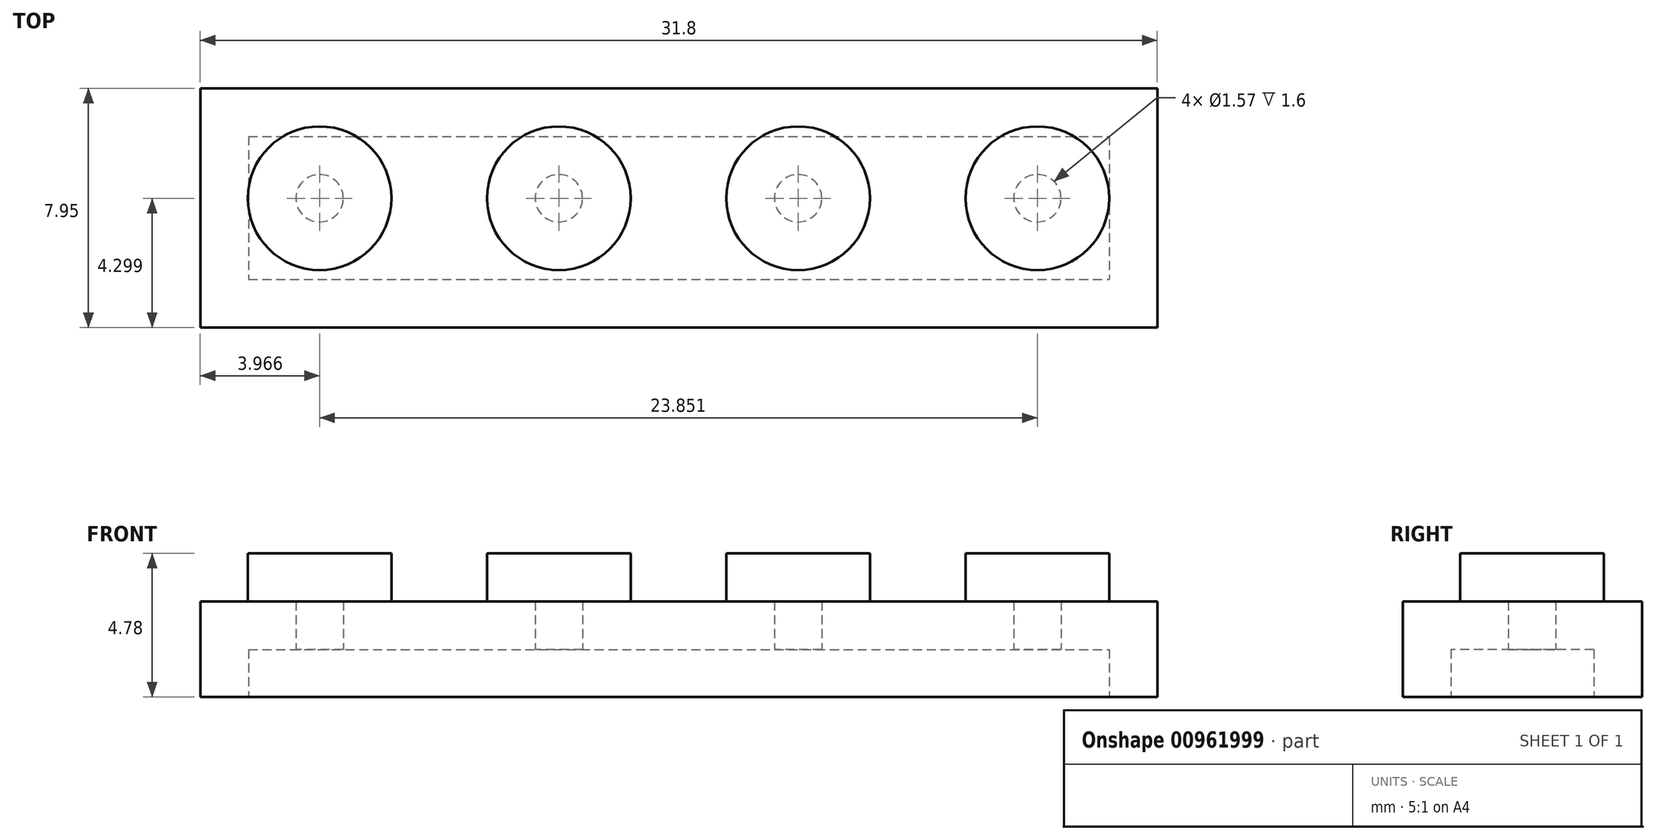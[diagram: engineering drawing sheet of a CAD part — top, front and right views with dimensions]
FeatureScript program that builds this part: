
annotation { "Feature Type Name" : "Feature", "Feature Type Description" : "" }
export const myFeature = defineFeature(function(context is Context, id is Id, definition is map)
    precondition{}
    {
        {
            var Q0;
            Q0=qCreatedBy(makeId("Top.planeOp"),FACE);
            var sketch = newSketch(context, id + "F0", { "sketchPlane" : qUnion([Q0])});
            skLineSegment(sketch, "E0.bottom", {"start": v(-20.76, 1.46) * mm, "end": v(11.04, 1.46) * mm});
            skLineSegment(sketch, "E0.top", {"start": v(-20.76, -6.49) * mm, "end": v(11.04, -6.49) * mm});
            skLineSegment(sketch, "E0.left", {"start": v(-20.76, 1.46) * mm, "end": v(-20.76, -6.49) * mm});
            skLineSegment(sketch, "E0.right", {"start": v(11.04, 1.46) * mm, "end": v(11.04, -6.49) * mm});
            skCircle(sketch, "E1", {"center": v(-16.8, -2.2) * mm, "radius": 2.39 * mm});
            skCircle(sketch, "E2.1.0.0", {"center": v(-8.84, -2.2) * mm, "radius": 2.39 * mm});
            skCircle(sketch, "E2.2.0.0", {"center": v(-0.9, -2.2) * mm, "radius": 2.39 * mm});
            skLineSegment(sketch, "E2.direction1", {"start": v(-16.8, -2.2) * mm, "end": v(-8.84, -2.2) * mm, "construction": true});
            skCircle(sketch, "E3.1.0.0", {"center": v(7.06, -2.2) * mm, "radius": 2.39 * mm});
            skLineSegment(sketch, "E3.direction1", {"start": v(-0.9, -2.2) * mm, "end": v(7.06, -2.2) * mm, "construction": true});
            skSolve(sketch);
        }
        {
            var Q0;
            Q0=makeQuery(id+"F0.imprint","IMPRINT",FACE,{"disambiguationData":[TD([[makeQuery(id+"F0.imprint","IMPRINT",EDGE,{"derivedFrom":sQuery(id+"F0.wireOp",EDGE,"E0.bottom")}),-1.0]])]});
            extrude(context, id + "F1", {"entities" : qUnion([Q0]), "depth" : 3.17 * mm, "offsetDistance" : 25.4 * mm});
        }
        {
            var Q0;
            Q0=makeQuery(id+"F0.imprint","IMPRINT",FACE,{"disambiguationData":[TD([[makeQuery(id+"F0.imprint","IMPRINT",EDGE,{"derivedFrom":sQuery(id+"F0.wireOp",EDGE,"E1")}),1.0]])]});
            var Q1;
            Q1=makeQuery(id+"F0.imprint","IMPRINT",FACE,{"disambiguationData":[TD([[makeQuery(id+"F0.imprint","IMPRINT",EDGE,{"derivedFrom":sQuery(id+"F0.wireOp",EDGE,"E2.1.0.0")}),1.0]])]});
            var Q2;
            Q2=makeQuery(id+"F0.imprint","IMPRINT",FACE,{"disambiguationData":[TD([[makeQuery(id+"F0.imprint","IMPRINT",EDGE,{"derivedFrom":sQuery(id+"F0.wireOp",EDGE,"E2.2.0.0")}),1.0]])]});
            var Q3;
            Q3=makeQuery(id+"F0.imprint","IMPRINT",FACE,{"disambiguationData":[TD([[makeQuery(id+"F0.imprint","IMPRINT",EDGE,{"derivedFrom":sQuery(id+"F0.wireOp",EDGE,"E3.1.0.0")}),1.0]])]});
            extrude(context, id + "F2", {"entities" : qUnion([Q0, Q1, Q2, Q3]), "operationType" : NewBodyOperationType.ADD, "depth" : 4.78 * mm, "offsetDistance" : 25.4 * mm});
        }
        {
            var Q0;
            {var subQ0=sQuery(id+"F0.wireOp",EDGE,"E3.1.0.0");var subQ1=sQuery(id+"F0.wireOp",EDGE,"E2.2.0.0");var subQ2=sQuery(id+"F0.wireOp",EDGE,"E2.1.0.0");var subQ3=sQuery(id+"F0.wireOp",EDGE,"E1");Q0=makeQuery(id+"F2.boolean.opBoolean","MERGE",FACE,{"derivedFrom":[makeQuery(id+"F1.opExtrude","CAP_FACE",FACE,{"disambiguationData":[OSD([sQuery(id+"F0.wireOp",EDGE,"E0.bottom"),sQuery(id+"F0.wireOp",EDGE,"E0.top"),sQuery(id+"F0.wireOp",EDGE,"E0.left"),sQuery(id+"F0.wireOp",EDGE,"E0.right"),subQ3,subQ2,subQ1,subQ0])],"isStart":true}),makeQuery(id+"F2.opExtrude","CAP_FACE",FACE,{"disambiguationData":[OSD([subQ3])],"isStart":true}),makeQuery(id+"F2.opExtrude","CAP_FACE",FACE,{"disambiguationData":[OSD([subQ2])],"isStart":true}),makeQuery(id+"F2.opExtrude","CAP_FACE",FACE,{"disambiguationData":[OSD([subQ1])],"isStart":true}),makeQuery(id+"F2.opExtrude","CAP_FACE",FACE,{"disambiguationData":[OSD([subQ0])],"isStart":true})]});}
            shell(context, id + "F3", {"entities" : qUnion([Q0]), "thickness" : 1.6 * mm});
        }
    });
